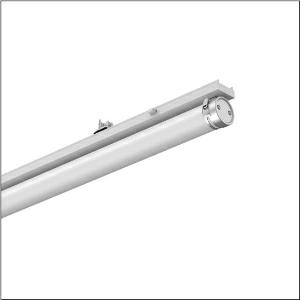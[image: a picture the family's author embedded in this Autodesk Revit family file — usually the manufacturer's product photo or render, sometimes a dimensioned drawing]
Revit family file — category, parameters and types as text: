
# Revit family: monsun_r__31_tube_51ft10nn4a0atr2_f2a8
name_source: partatom
category: Lighting Fixtures
units: mm (PartAtom-declared; Revit-internal decimal feet)

## family parameters
Cut with Voids When Loaded = No
Host = Face
Light Source = No
Part Type = Normal
Room Calculation Point = No
Round Connector Dimension = Use Diameter
Shared = No

## types (1)
- --- (1 x LED, 10000 lm, 58 W, 4000K)
    Apparent Load = 58 VA
    CIE Flux Codes = 42 71 90 91 100
    Color Rendering = 80
    Color Temperature = 4000K
    Default Elevation = 1800 mm
    Description = Monsun® 31 Tube, tubular luminaire, primary optical cover: diffuser, of PMMA, light emission: direct distribution, primary light characteristic: symmetric, LED, rated luminous flux: 10.000lm, luminous efficacy: 172lm/W, light colour: 840, colour temperature: 4000K, with with 1 terminal, 5-pole, max. 2.5mm², mains connection: 220..240V, AC, 50/60Hz, rated input power: 58W, housing, cylindrical, of PMMA, semi-transparent, matt white, with luminaire and ceiling fastening, V4A, mounting with brackets of stainless steel, length: 1.500mm, diameter: 75mm, end cap, of stainless steel (V4A), protection rating (complete): IP20, protection rating (lamp compartment): IP67/69K, insulation class (complete): insulation class I (protective earthing), certification: CE, UKCA, impact resistance: IK06, permissible operating ambient temperature: -20..+40°C, corresponds to IFS (International Featured Standards) requirements for safety and quality in the food industry, contact your sales advisor before using the luminaires in applications with unclear chemical exposure, large temperature fluctuations or condensation-forming humidity, packaging unit: 1 piece
    Height = 132 mm
    Lamp = 1 x LED
    Lamp Light Flux = 10000 lm
    Lamp Power = 58 W
    Lamp count = 1
    Length = 1500 mm
    Luminous efficacy = 172 lm/W
    Manufacturer = Siteco
    ModVariant = No
    Model = 51FT10NN4A0ATR2
    Mounting Place = Ceiling
    Mounting Type = Pendant
    Number of Poles = 1
    OnlyDefault = Yes
    Power Factor = 1
    Product Name = Monsun® 31 Tube
    Product group = tubular luminaire
    ProductGroupID = 906
    Protection Class = Protection class I
    Protection Degree = IP 20
    RLX_Detail_Level = 1
    RLX_Emergency_Light_Flux = 0 lm
    RLX_Emergency_Type = 0
    RLX_Emergency_Type_DB = No
    RlxData = <blob elided: 32277 chars, md5=17a76399>
    Socket = socket
    Standby Power = 0 W
    System Light Flux = 10000 lm
    System Power = 58 W
    Type Comments = individual setting: luminous flux: 100 % | (OFF | OFF | ON | OFF) | 350 mA
    Type Image = l_1242814.jpg
    URL = http://relux.com
    VarID = @adj_113157
    Voltage = 0 V
    Weight = 0.00 kg
    Width = 79 mm

## geometry (parser evidence)
native form markers: Blend x4, Sweep x11
no freeform markers — native parametric forms only
